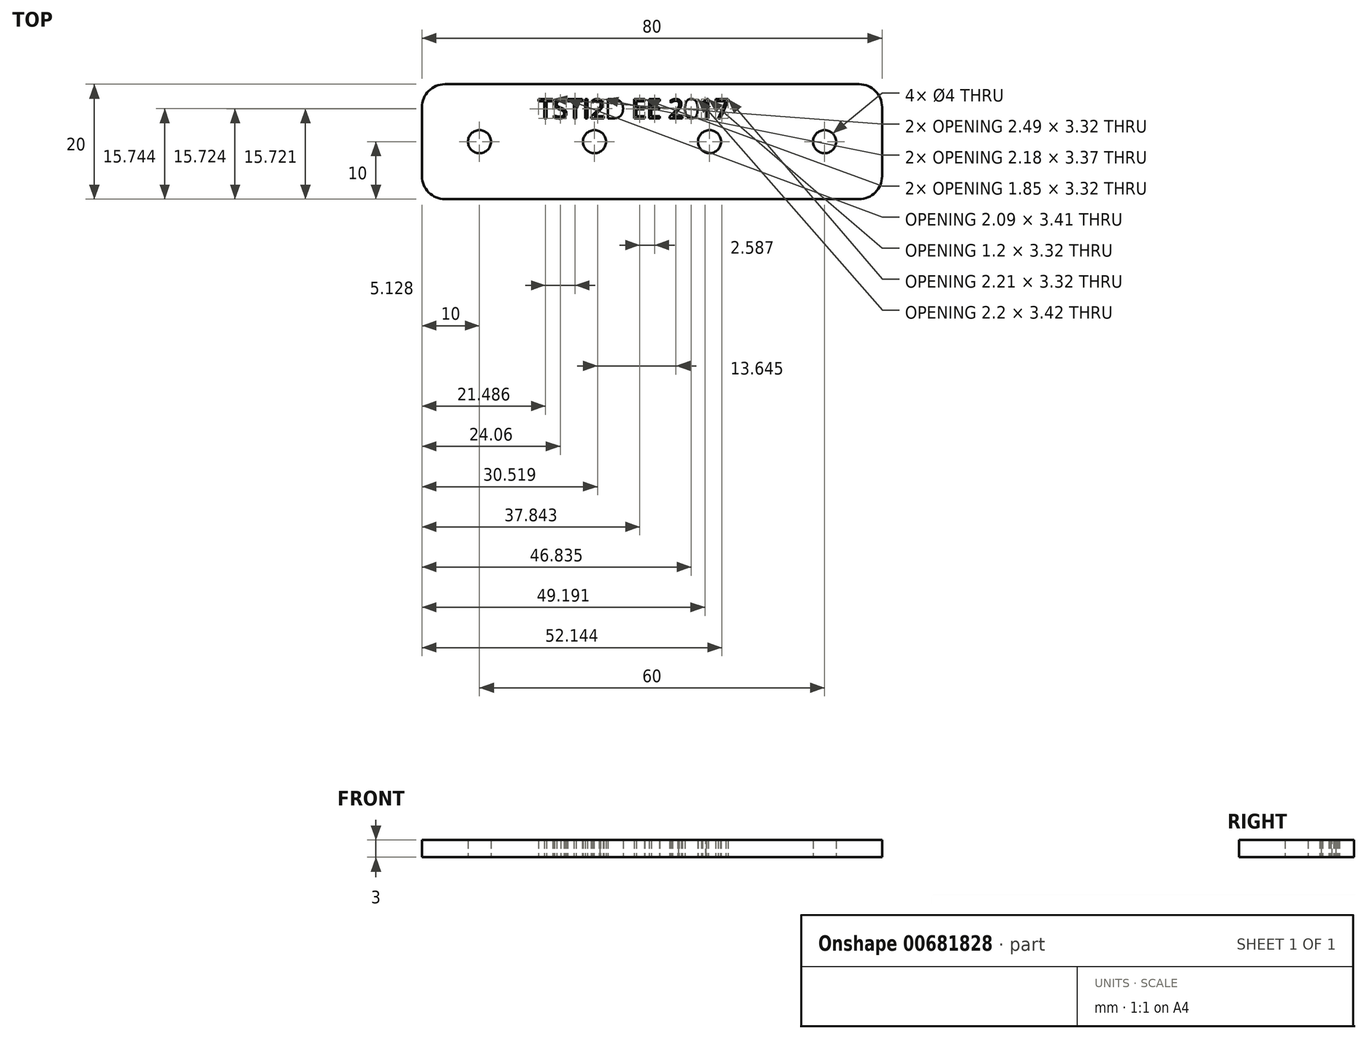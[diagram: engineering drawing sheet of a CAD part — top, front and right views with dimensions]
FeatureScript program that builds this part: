
annotation { "Feature Type Name" : "Feature", "Feature Type Description" : "" }
export const myFeature = defineFeature(function(context is Context, id is Id, definition is map)
    precondition{}
    {
        {
            var Q0;
            Q0=qCreatedBy(makeId("Top.planeOp"),FACE);
            var sketch = newSketch(context, id + "F0", { "sketchPlane" : qUnion([Q0])});
            skLineSegment(sketch, "E0.bottom", {"start": v(-36, 10) * mm, "end": v(36, 10) * mm});
            skLineSegment(sketch, "E0.top", {"start": v(-36, -10) * mm, "end": v(36, -10) * mm});
            skLineSegment(sketch, "E0.left", {"start": v(-40, 6) * mm, "end": v(-40, -6) * mm});
            skLineSegment(sketch, "E0.right", {"start": v(40, 6) * mm, "end": v(40, -6) * mm});
            skCircle(sketch, "E1", {"center": v(-30, 0) * mm, "radius": 2 * mm});
            skCircle(sketch, "E2.1.0.0", {"center": v(-10, 0) * mm, "radius": 2 * mm});
            skCircle(sketch, "E2.2.0.0", {"center": v(10, 0) * mm, "radius": 2 * mm});
            skCircle(sketch, "E2.3.0.0", {"center": v(30, 0) * mm, "radius": 2 * mm});
            skLineSegment(sketch, "E2.direction1", {"start": v(-30, 0) * mm, "end": v(-10, 0) * mm, "construction": true});
            skPoint(sketch, "E3.visualSharp", {"position": v(-40, 10) * mm});
            skArc(sketch, "E3.filletArc", {"start": v(-36, 10) * mm, "mid": v(-38.83, 8.83) * mm, "end": v(-40, 6) * mm});
            skPoint(sketch, "E4.visualSharp", {"position": v(-40, -10) * mm});
            skArc(sketch, "E4.filletArc", {"start": v(-40, -6) * mm, "mid": v(-38.83, -8.83) * mm, "end": v(-36, -10) * mm});
            skPoint(sketch, "E5.visualSharp", {"position": v(40, 10) * mm});
            skArc(sketch, "E5.filletArc", {"start": v(40, 6) * mm, "mid": v(38.83, 8.83) * mm, "end": v(36, 10) * mm});
            skPoint(sketch, "E6.visualSharp", {"position": v(40, -10) * mm});
            skArc(sketch, "E6.filletArc", {"start": v(36, -10) * mm, "mid": v(38.83, -8.83) * mm, "end": v(40, -6) * mm});
            skText(sketch, "E7", { "text": "TSTI2D EE 2017", "fontName": "OpenSans-Regular.ttf"});
            const initialGuessF0  = {"E7": [-0.0198, 0.00406, 1, 0, 0.00335]};
            skSetInitialGuess(sketch, initialGuessF0);
            skSolve(sketch);
        }
        {
            var Q0;
            Q0 = qSketchRegion(id + "F0", true);
            extrude(context, id + "F1", {"entities" : qUnion([Q0]), "depth" : 3 * mm, "offsetDistance" : 25 * mm});
        }
    });
